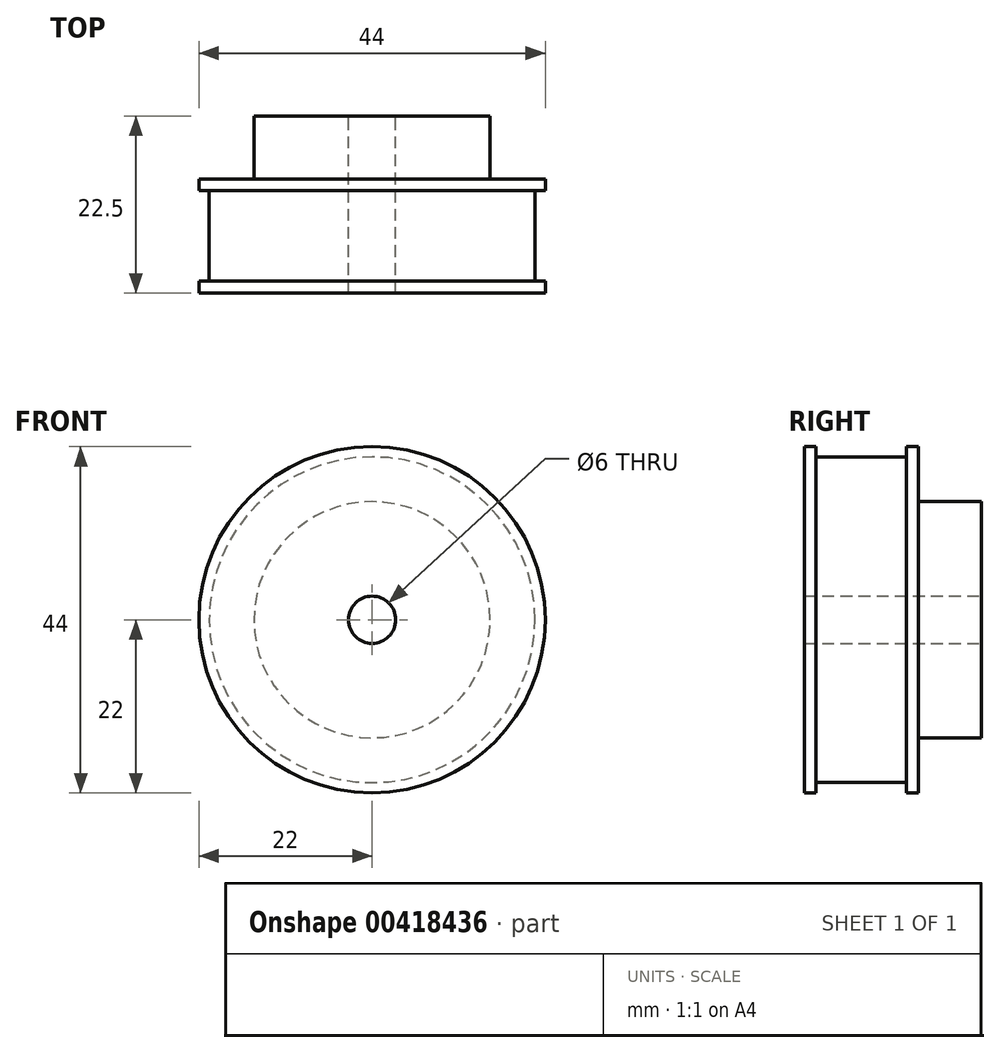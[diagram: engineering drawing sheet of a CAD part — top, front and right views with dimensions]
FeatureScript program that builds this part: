
annotation { "Feature Type Name" : "Feature", "Feature Type Description" : "" }
export const myFeature = defineFeature(function(context is Context, id is Id, definition is map)
    precondition{}
    {
        {
            var Q0;
            Q0=qCreatedBy(makeId("Front.planeOp"),FACE);
            var sketch = newSketch(context, id + "F0", { "sketchPlane" : qUnion([Q0])});
            skCircle(sketch, "E0", {"center": v(0, 0) * mm, "radius": 22 * mm});
            skSolve(sketch);
        }
        {
            var Q0;
            Q0 = qSketchRegion(id + "F0", true);
            extrude(context, id + "F1", {"entities" : qUnion([Q0]), "depth" : 1.5 * mm});
        }
        {
            var Q0;
            Q0=makeQuery(id+"F1.opExtrude","CAP_FACE",FACE,{"disambiguationData":[OSD([sQuery(id+"F0.wireOp",EDGE,"E0")])],"isStart":true});
            var sketch = newSketch(context, id + "F2", { "sketchPlane" : qUnion([Q0])});
            skCircle(sketch, "E1", {"center": v(0, 0) * mm, "radius": 20.7 * mm});
            skSolve(sketch);
        }
        {
            var Q0;
            Q0 = qSketchRegion(id + "F2", true);
            extrude(context, id + "F3", {"entities" : qUnion([Q0]), "operationType" : NewBodyOperationType.ADD, "depth" : 11.5 * mm});
        }
        {
            var Q0;
            Q0=makeQuery(id+"F3.opExtrude","CAP_FACE",FACE,{"disambiguationData":[OSD([sQuery(id+"F2.wireOp",EDGE,"E1")])],"isStart":false});
            var sketch = newSketch(context, id + "F4", { "sketchPlane" : qUnion([Q0])});
            skCircle(sketch, "E2", {"center": v(0, 0) * mm, "radius": 22 * mm});
            skSolve(sketch);
        }
        {
            var Q0;
            Q0 = qSketchRegion(id + "F4", true);
            extrude(context, id + "F5", {"entities" : qUnion([Q0]), "operationType" : NewBodyOperationType.ADD, "depth" : 1.5 * mm});
        }
        {
            var Q0;
            Q0=makeQuery(id+"F5.opExtrude","CAP_FACE",FACE,{"disambiguationData":[OSD([sQuery(id+"F4.wireOp",EDGE,"E2")])],"isStart":false});
            var sketch = newSketch(context, id + "F6", { "sketchPlane" : qUnion([Q0])});
            skCircle(sketch, "E3", {"center": v(0, 0) * mm, "radius": 15 * mm});
            skSolve(sketch);
        }
        {
            var Q0;
            Q0 = qSketchRegion(id + "F6", true);
            extrude(context, id + "F7", {"entities" : qUnion([Q0]), "operationType" : NewBodyOperationType.ADD, "depth" : (22.5 - 14.5) * mm});
        }
        {
            var Q0;
            Q0=makeQuery(id+"F7.opExtrude","CAP_FACE",FACE,{"disambiguationData":[OSD([sQuery(id+"F6.wireOp",EDGE,"E3")])],"isStart":false});
            var sketch = newSketch(context, id + "F8", { "sketchPlane" : qUnion([Q0])});
            skCircle(sketch, "E4", {"center": v(0, 0) * mm, "radius": 3 * mm});
            skSolve(sketch);
        }
        {
            var Q0;
            Q0 = qSketchRegion(id + "F8", true);
            extrude(context, id + "F9", {"entities" : qUnion([Q0]), "operationType" : NewBodyOperationType.REMOVE, "endBound" : BoundingType.THROUGH_ALL, "oppositeDirection" : true, "depth" : 25 * mm});
        }
    });
